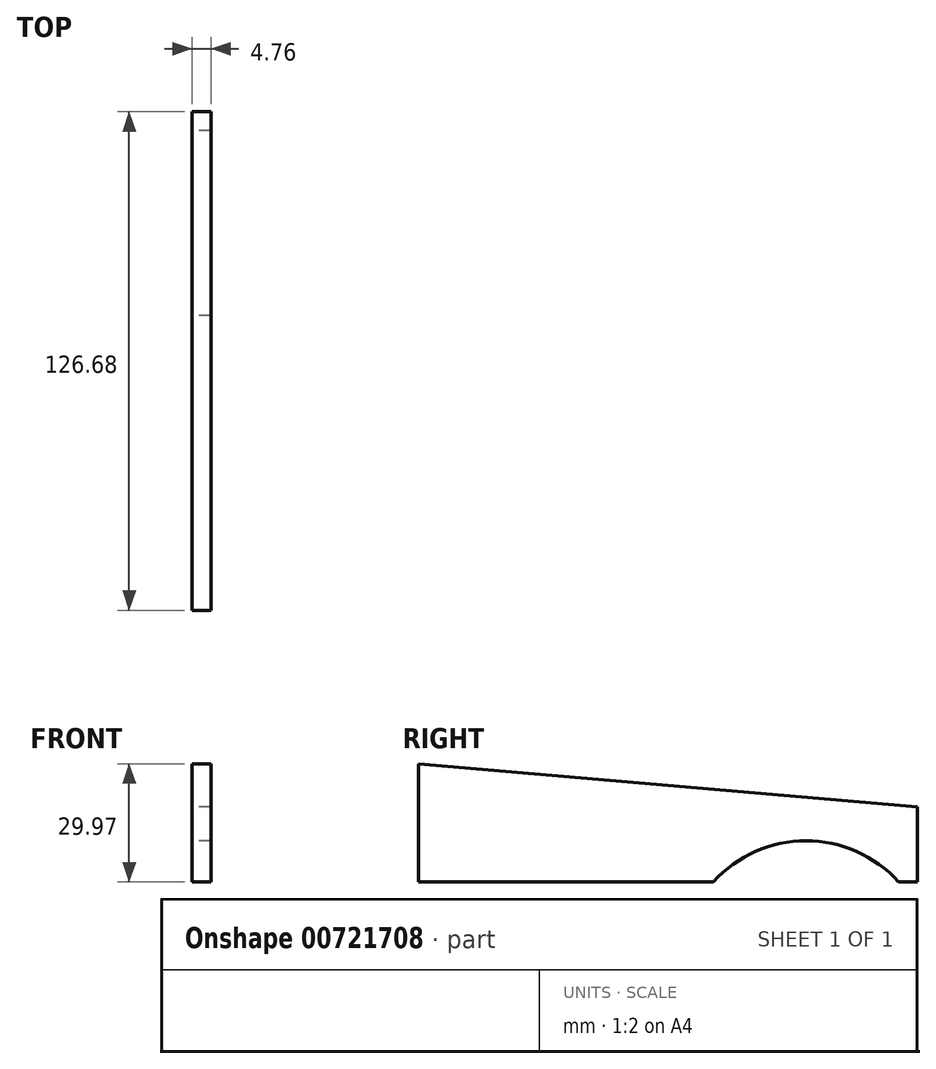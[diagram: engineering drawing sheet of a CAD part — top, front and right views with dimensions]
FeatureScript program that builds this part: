
annotation { "Feature Type Name" : "Feature", "Feature Type Description" : "" }
export const myFeature = defineFeature(function(context is Context, id is Id, definition is map)
    precondition{}
    {
        {
            var Q0;
            Q0=qCreatedBy(makeId("Right.planeOp"),FACE);
            var sketch = newSketch(context, id + "F0", { "sketchPlane" : qUnion([Q0])});
            skLineSegment(sketch, "E0", {"start": v(126.68, 19.05) * mm, "end": v(0, 29.97) * mm});
            skLineSegment(sketch, "E1", {"start": v(126.68, 19.05) * mm, "end": v(126.68, 0) * mm});
            skLineSegment(sketch, "E2", {"start": v(126.68, 0) * mm, "end": v(121.92, 0) * mm});
            skLineSegment(sketch, "E3", {"start": v(0, 0) * mm, "end": v(0, 29.97) * mm});
            skArc(sketch, "E4", {"start": v(121.92, 0) * mm, "mid": v(98.43, 10.4) * mm, "end": v(74.93, 0) * mm});
            skLineSegment(sketch, "E5.trimOffspring", {"start": v(74.93, 0) * mm, "end": v(0, 0) * mm});
            skSolve(sketch);
        }
        {
            var Q0;
            Q0=qSketchRegion(id+"F0",true);
            extrude(context, id + "F1", {"entities" : qUnion([Q0]), "depth" : 4.76 * mm, "offsetDistance" : 25.4 * mm});
        }
    });
